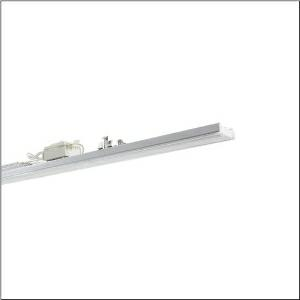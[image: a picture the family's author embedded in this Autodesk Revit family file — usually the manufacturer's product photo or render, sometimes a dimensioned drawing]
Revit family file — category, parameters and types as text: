
# Revit family: licross_r__21_recessed_mo_52te19dv4e5g_2993
name_source: partatom
category: Lighting Fixtures
units: mm (PartAtom-declared; Revit-internal decimal feet)

## family parameters
Cut with Voids When Loaded = No
Host = Face
Light Source = No
Part Type = Normal
Room Calculation Point = No
Round Connector Dimension = Use Diameter
Shared = No

## types (1)
- --- (1 x LED, 14780 lm, 85.3 W, 4000K)
    Apparent Load = 85 VA
    CIE Flux Codes = 55 90 98 100 100
    Color Rendering = 80
    Color Temperature = 4000K
    Default Elevation = 1800 mm
    Description = Licross® 21 Recessed MO, luminaire insert, of sheet steel, galvanised, coil coated, white, length: 2.250mm, width: 66mm, height: 67mm, LED rated luminous flux: 14.780lm, light colour: 840, control gear: DALI 2, with plug, 5-pole, with phase selection, mains connection: 220..240V, AC, 50/60Hz, rated input power: 85W, halogen-free wiring, primary light control with lens, of plastic, primary optical cover: cover, of PMMA, light emission: direct distribution, primary light characteristic: double asymmetric, protection rating (complete): IP54, insulation class (complete): insulation class I (protective earthing), certification: CE, ENEC, VDE, UKCA, protection symbol: D if used in an environment with non-conductive dust loads with corresponding accessories, impact resistance: IK06, permissible ambient temperature for indoor applications: -25..+35°C, corresponds to IFS (International Featured Standards) requirements for safety and quality in the food industry, reducing of maximum allowable ambient temperature of 5°C with ceiling mounting, LABS conformity tested according to VDMA 24364:2018-05, packaging unit: 1 piece
    Height = 58 mm
    Lamp = 1 x LED
    Lamp Light Flux = 14780 lm
    Lamp Power = 85.3 W
    Lamp count = 1
    Length = 2250 mm
    Luminous efficacy = 173 lm/W
    Manufacturer = Siteco
    ModVariant = No
    Model = 52TE19DV4E5G
    Mounting Place = Ceiling
    Mounting Type = Pendant
    Number of Poles = 1
    OnlyDefault = Yes
    Power Factor = 1
    Product Name = Licross® 21 Recessed MO
    Product group = luminaire insert
    ProductGroupID = 902
    Protection Class = Protection class I
    Protection Degree = IP 54
    RLX_Detail_Level = 1
    RLX_Emergency_Light_Flux = 0 lm
    RLX_Emergency_Type = 0
    RLX_Emergency_Type_DB = No
    RlxData = <blob elided: 29497 chars, md5=e018c3a2>
    Socket = socket
    Standby Power = 0 W
    System Light Flux = 14780 lm
    System Power = 85 W
    Type Comments = factory setting: luminous flux: 100 % | dim-lin: 254 | 390 mA
    Type Image = l_1296930.jpg
    URL = http://relux.com
    VarID = @adj_128008
    Voltage = 0 V
    Weight = 0.00 kg
    Width = 66 mm

## geometry (parser evidence)
native form markers: Blend x4, Sweep x10
no freeform markers — native parametric forms only
